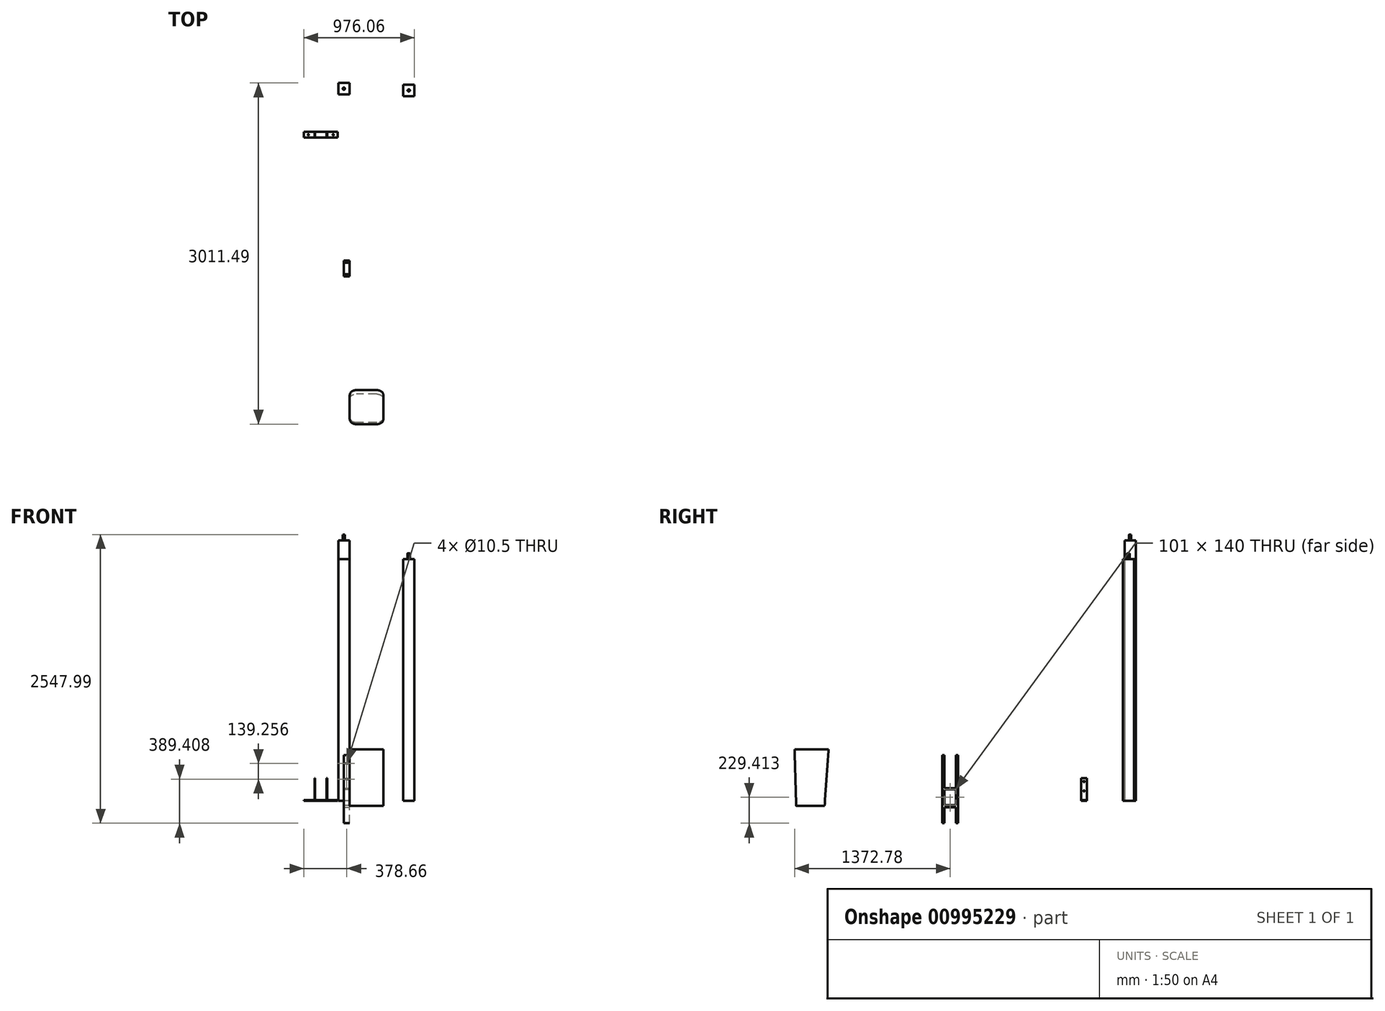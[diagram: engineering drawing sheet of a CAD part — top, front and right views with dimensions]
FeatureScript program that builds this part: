
annotation { "Feature Type Name" : "Feature", "Feature Type Description" : "" }
export const myFeature = defineFeature(function(context is Context, id is Id, definition is map)
    precondition{}
    {
        {
            var Q0;
            Q0=qCreatedBy(makeId("Top.planeOp"),FACE);
            var sketch = newSketch(context, id + "F0", { "sketchPlane" : qUnion([Q0])});
            skLineSegment(sketch, "E0.bottom", {"start": v(50, -50) * mm, "end": v(-50, -50) * mm});
            skLineSegment(sketch, "E0.top", {"start": v(50, 50) * mm, "end": v(-50, 50) * mm});
            skLineSegment(sketch, "E0.left", {"start": v(50, -50) * mm, "end": v(50, 50) * mm});
            skLineSegment(sketch, "E0.right", {"start": v(-50, -50) * mm, "end": v(-50, 50) * mm});
            skPoint(sketch, "E0.middle", {"position": v(0, 0) * mm});
            skLineSegment(sketch, "E1.bottom", {"start": v(522.4, 34.47) * mm, "end": v(622.4, 34.47) * mm});
            skLineSegment(sketch, "E1.top", {"start": v(522.4, -65.53) * mm, "end": v(622.4, -65.53) * mm});
            skLineSegment(sketch, "E1.left", {"start": v(522.4, 34.47) * mm, "end": v(522.4, -65.53) * mm});
            skLineSegment(sketch, "E1.right", {"start": v(622.4, 34.47) * mm, "end": v(622.4, -65.53) * mm});
            skSolve(sketch);
        }
        {
            var Q0;
            Q0=makeQuery(id+"F0.imprint","IMPRINT",FACE,{"disambiguationData":[TD([[makeQuery(id+"F0.imprint","IMPRINT",EDGE,{"derivedFrom":sQuery(id+"F0.wireOp",EDGE,"E0.bottom")}),-1.0]])]});
            extrude(context, id + "F1", {"entities" : qUnion([Q0]), "depth" : 2300 * mm, "offsetDistance" : 25 * mm});
        }
        {
            var Q0;
            Q0 = qSketchRegion(id + "F0", true);
            extrude(context, id + "F2", {"entities" : qUnion([Q0]), "depth" : 2135 * mm, "offsetDistance" : 25 * mm});
        }
        {
            var Q0;
            Q0=makeQuery(id+"F1.opExtrude","CAP_FACE",FACE,{"disambiguationData":[OSD([sQuery(id+"F0.wireOp",EDGE,"E0.bottom"),sQuery(id+"F0.wireOp",EDGE,"E0.top"),sQuery(id+"F0.wireOp",EDGE,"E0.left"),sQuery(id+"F0.wireOp",EDGE,"E0.right")])],"isStart":false});
            var sketch = newSketch(context, id + "F3", { "sketchPlane" : qUnion([Q0])});
            skCircle(sketch, "E2", {"center": v(0, 0) * mm, "radius": 10 * mm});
            skSolve(sketch);
        }
        {
            var Q0;
            Q0=makeQuery(id+"F3.imprint","IMPRINT",FACE,{"disambiguationData":[TD([[makeQuery(id+"F3.imprint","IMPRINT",EDGE,{"derivedFrom":sQuery(id+"F3.wireOp",EDGE,"E2")}),1.0]])]});
            extrude(context, id + "F4", {"entities" : qUnion([Q0]), "operationType" : NewBodyOperationType.ADD, "depth" : 50 * mm, "offsetDistance" : 25 * mm});
        }
        {
            var Q0;
            Q0=makeQuery(id+"F2.opExtrude","CAP_FACE",FACE,{"disambiguationData":[OSD([sQuery(id+"F0.wireOp",EDGE,"E1.bottom"),sQuery(id+"F0.wireOp",EDGE,"E1.top"),sQuery(id+"F0.wireOp",EDGE,"E1.left"),sQuery(id+"F0.wireOp",EDGE,"E1.right")])],"isStart":false});
            var sketch = newSketch(context, id + "F5", { "sketchPlane" : qUnion([Q0])});
            skCircle(sketch, "E3", {"center": v(572.4, -15.53) * mm, "radius": 10 * mm});
            skPoint(sketch, "E3.centerSnap0", {"position": v(522.4, -15.53) * mm});
            skPoint(sketch, "E3.centerSnap1", {"position": v(572.4, -65.53) * mm});
            skSolve(sketch);
        }
        {
            var Q0;
            Q0 = qSketchRegion(id + "F5", true);
            extrude(context, id + "F6", {"entities" : qUnion([Q0]), "operationType" : NewBodyOperationType.ADD, "depth" : 50 * mm, "offsetDistance" : 25 * mm});
        }
        {
            var Q0;
            Q0=qCreatedBy(makeId("Right.planeOp"),FACE);
            var sketch = newSketch(context, id + "F7", { "sketchPlane" : qUnion([Q0])});
            skLineSegment(sketch, "E4.bottom", {"start": v(-1658.7, 402.01) * mm, "end": v(-1518.7, 402.01) * mm});
            skLineSegment(sketch, "E4.top", {"start": v(-1658.7, -197.99) * mm, "end": v(-1518.7, -197.99) * mm});
            skLineSegment(sketch, "E4.left", {"start": v(-1658.7, 402.01) * mm, "end": v(-1658.7, -197.99) * mm});
            skLineSegment(sketch, "E4.right", {"start": v(-1518.7, 402.01) * mm, "end": v(-1518.7, -197.99) * mm});
            skSolve(sketch);
        }
        {
            var Q0;
            Q0=makeQuery(id+"F7.imprint","IMPRINT",FACE,{"disambiguationData":[TD([[makeQuery(id+"F7.imprint","IMPRINT",EDGE,{"derivedFrom":sQuery(id+"F7.wireOp",EDGE,"E4.bottom")}),-1.0]])]});
            extrude(context, id + "F8", {"entities" : qUnion([Q0]), "depth" : 50 * mm, "offsetDistance" : 25 * mm});
        }
        {
            var Q0;
            Q0=makeQuery(id+"F8.opExtrude","CAP_FACE",FACE,{"disambiguationData":[OSD([sQuery(id+"F7.wireOp",EDGE,"E4.bottom"),sQuery(id+"F7.wireOp",EDGE,"E4.top"),sQuery(id+"F7.wireOp",EDGE,"E4.left"),sQuery(id+"F7.wireOp",EDGE,"E4.right")])],"isStart":false});
            var sketch = newSketch(context, id + "F9", { "sketchPlane" : qUnion([Q0])});
            skLineSegment(sketch, "E5", {"start": v(-1588.7, 427.22) * mm, "end": v(-1588.7, -231.36) * mm, "construction": true});
            skPoint(sketch, "E5.startSnap0", {"position": v(-1588.7, 402.01) * mm});
            skLineSegment(sketch, "E6", {"start": v(-1690.33, 102.01) * mm, "end": v(-1494.55, 102.01) * mm, "construction": true});
            skPoint(sketch, "E6.startSnap0", {"position": v(-1658.7, 102.01) * mm});
            skPoint(sketch, "E7.middle", {"position": v(-1588.7, 284.64) * mm});
            skLineSegment(sketch, "E8", {"start": v(-1639.2, 402.01) * mm, "end": v(-1639.2, 111.41) * mm});
            skLineSegment(sketch, "E9", {"start": v(-1639.2, 111.41) * mm, "end": v(-1538.2, 111.41) * mm});
            skLineSegment(sketch, "E10", {"start": v(-1538.2, 111.41) * mm, "end": v(-1538.2, 402.01) * mm});
            skLineSegment(sketch, "E11", {"start": v(-1538.2, 402.01) * mm, "end": v(-1639.2, 402.01) * mm});
            skLineSegment(sketch, "E12", {"start": v(-1588.7, 418.52) * mm, "end": v(-1588.7, 132.47) * mm, "construction": true});
            skLineSegment(sketch, "E13", {"start": v(-1639.2, -197.99) * mm, "end": v(-1639.2, -57.99) * mm});
            skLineSegment(sketch, "E14", {"start": v(-1639.2, -57.99) * mm, "end": v(-1538.2, -57.99) * mm});
            skLineSegment(sketch, "E15", {"start": v(-1538.2, -57.99) * mm, "end": v(-1538.2, -197.99) * mm});
            skLineSegment(sketch, "E16", {"start": v(-1588.7, -57.99) * mm, "end": v(-1588.7, -234) * mm, "construction": true});
            skLineSegment(sketch, "E17.bottom", {"start": v(-1639.2, 101.42) * mm, "end": v(-1538.2, 101.42) * mm});
            skLineSegment(sketch, "E17.top", {"start": v(-1639.2, -38.58) * mm, "end": v(-1538.2, -38.58) * mm});
            skLineSegment(sketch, "E17.left", {"start": v(-1639.2, 101.42) * mm, "end": v(-1639.2, -38.58) * mm});
            skLineSegment(sketch, "E17.right", {"start": v(-1538.2, 101.42) * mm, "end": v(-1538.2, -38.58) * mm});
            skLineSegment(sketch, "E18", {"start": v(-1588.7, 101.42) * mm, "end": v(-1588.7, -38.58) * mm, "construction": true});
            skLineSegment(sketch, "E19", {"start": v(-2961.49, 454.13) * mm, "end": v(-2661.49, 454.13) * mm});
            skLineSegment(sketch, "E20", {"start": v(-2661.49, 454.13) * mm, "end": v(-2696.45, -45.87) * mm});
            skLineSegment(sketch, "E21", {"start": v(-2696.45, -45.87) * mm, "end": v(-2946.45, -45.87) * mm});
            skLineSegment(sketch, "E22", {"start": v(-2946.45, -45.87) * mm, "end": v(-2961.49, 454.13) * mm});
            skSolve(sketch);
        }
        {
            var Q0;
            Q0=makeQuery(id+"F9.imprint","IMPRINT",FACE,{"disambiguationData":[TD([[makeQuery(id+"F9.imprint","IMPRINT",EDGE,{"derivedFrom":sQuery(id+"F9.wireOp",EDGE,"E8")}),1.0]])]});
            var Q1;
            Q1=makeQuery(id+"F9.imprint","IMPRINT",FACE,{"disambiguationData":[TD([[makeQuery(id+"F9.imprint","IMPRINT",EDGE,{"derivedFrom":sQuery(id+"F9.wireOp",EDGE,"E17.bottom")}),-1.0]])]});
            var Q2;
            {var subQ0=sQuery(id+"F9.wireOp",EDGE,"E13");Q2=makeQuery(id+"F9.imprint","IMPRINT",FACE,{"disambiguationData":[TD([[makeQuery(id+"F9.imprint","IMPRINT",EDGE,{"derivedFrom":subQ0}),-1.0]])]});}
            extrude(context, id + "F10", {"entities" : qUnion([Q0, Q1, Q2]), "operationType" : NewBodyOperationType.REMOVE, "endBound" : BoundingType.THROUGH_ALL, "oppositeDirection" : true, "depth" : 25 * mm, "offsetDistance" : 25 * mm});
        }
        {
            var Q0;
            Q0=makeQuery(id+"F9.imprint","IMPRINT",FACE,{"disambiguationData":[TD([[makeQuery(id+"F9.imprint","IMPRINT",EDGE,{"derivedFrom":sQuery(id+"F9.wireOp",EDGE,"E19")}),-1.0]])]});
            extrude(context, id + "F11", {"entities" : qUnion([Q0]), "depth" : 300 * mm, "offsetDistance" : 25 * mm});
        }
        {
            var Q0;
            Q0=makeQuery(id+"F11.opExtrude","CAP_EDGE",EDGE,{"disambiguationData":[OSD([sQuery(id+"F9.wireOp",EDGE,"E22")])],"isStart":false});
            var Q1;
            Q1=makeQuery(id+"F11.opExtrude","CAP_EDGE",EDGE,{"disambiguationData":[OSD([sQuery(id+"F9.wireOp",EDGE,"E22")])],"isStart":true});
            var Q2;
            Q2=makeQuery(id+"F11.opExtrude","CAP_EDGE",EDGE,{"disambiguationData":[OSD([sQuery(id+"F9.wireOp",EDGE,"E20")])],"isStart":true});
            var Q3;
            Q3=makeQuery(id+"F11.opExtrude","CAP_EDGE",EDGE,{"disambiguationData":[OSD([sQuery(id+"F9.wireOp",EDGE,"E20")])],"isStart":false});
            fillet(context, id + "F12", {"entities" : qUnion([Q0, Q1, Q2, Q3]), "radius" : 60 * mm, "rho" : 0.5, "crossSection" : FilletCrossSection.CONIC, "allowEdgeOverflow" : false});
        }
        {
            var Q0;
            Q0=makeQuery(id+"F8.opExtrude","SWEPT_FACE",FACE,{"disambiguationData":[OSD([sQuery(id+"F7.wireOp",EDGE,"E4.left")])]});
            var sketch = newSketch(context, id + "F13", { "sketchPlane" : qUnion([Q0])});
            skPoint(sketch, "E23.centerSnap0", {"position": v(25, 402.01) * mm});
            skPoint(sketch, "E24", {"position": v(25, 330.67) * mm});
            skPoint(sketch, "E25", {"position": v(25, 191.42) * mm});
            skSolve(sketch);
        }
        {
            var Q0;
            Q0=qCreatedBy(makeId("Top.planeOp"),FACE);
            var sketch = newSketch(context, id + "F14", { "sketchPlane" : qUnion([Q0])});
            skLineSegment(sketch, "E26.bottom", {"start": v(-53.66, -432.35) * mm, "end": v(-353.66, -432.35) * mm});
            skLineSegment(sketch, "E26.top", {"start": v(-53.66, -382.35) * mm, "end": v(-353.66, -382.35) * mm});
            skLineSegment(sketch, "E26.left", {"start": v(-53.66, -432.35) * mm, "end": v(-53.66, -382.35) * mm});
            skLineSegment(sketch, "E26.right", {"start": v(-353.66, -432.35) * mm, "end": v(-353.66, -382.35) * mm});
            skPoint(sketch, "E26.middle", {"position": v(-203.66, -407.35) * mm});
            skPoint(sketch, "E27", {"position": v(-313.66, -407.35) * mm});
            skPoint(sketch, "E27.positionSnap0", {"position": v(-353.66, -407.35) * mm});
            skPoint(sketch, "E28", {"position": v(-93.66, -407.35) * mm});
            skSolve(sketch);
        }
        {
            var Q0;
            Q0=makeQuery(id+"F14.imprint","IMPRINT",FACE,{"disambiguationData":[TD([[makeQuery(id+"F14.imprint","IMPRINT",EDGE,{"derivedFrom":sQuery(id+"F14.wireOp",EDGE,"E26.bottom")}),-1.0]])]});
            extrude(context, id + "F15", {"entities" : qUnion([Q0]), "depth" : 200 * mm, "offsetDistance" : 25 * mm});
        }
        {
            var Q0;
            Q0=makeQuery(id+"F15.opExtrude","SWEPT_FACE",FACE,{"disambiguationData":[OSD([sQuery(id+"F14.wireOp",EDGE,"E26.bottom")])]});
            var sketch = newSketch(context, id + "F16", { "sketchPlane" : qUnion([Q0])});
            skLineSegment(sketch, "E29.bottom", {"start": v(-353.66, 200) * mm, "end": v(-259.16, 200) * mm});
            skLineSegment(sketch, "E29.top", {"start": v(-353.66, 5) * mm, "end": v(-259.16, 5) * mm});
            skLineSegment(sketch, "E29.left", {"start": v(-353.66, 200) * mm, "end": v(-353.66, 5) * mm});
            skLineSegment(sketch, "E29.right", {"start": v(-259.16, 200) * mm, "end": v(-259.16, 5) * mm});
            skLineSegment(sketch, "E30.bottom", {"start": v(-53.66, 200) * mm, "end": v(-148.16, 200) * mm});
            skLineSegment(sketch, "E30.top", {"start": v(-53.66, 5) * mm, "end": v(-148.16, 5) * mm});
            skLineSegment(sketch, "E30.left", {"start": v(-53.66, 200) * mm, "end": v(-53.66, 5) * mm});
            skLineSegment(sketch, "E30.right", {"start": v(-148.16, 200) * mm, "end": v(-148.16, 5) * mm});
            skLineSegment(sketch, "E31.bottom", {"start": v(-254.16, 200) * mm, "end": v(-153.16, 200) * mm});
            skLineSegment(sketch, "E31.top", {"start": v(-254.16, 5) * mm, "end": v(-153.16, 5) * mm});
            skLineSegment(sketch, "E31.left", {"start": v(-153.16, 200) * mm, "end": v(-153.16, 5) * mm});
            skLineSegment(sketch, "E31.right", {"start": v(-254.16, 200) * mm, "end": v(-254.16, 5) * mm});
            skLineSegment(sketch, "E32", {"start": v(-203.66, 200) * mm, "end": v(-203.66, 0) * mm, "construction": true});
            skLineSegment(sketch, "E33", {"start": v(-203.66, 200) * mm, "end": v(-203.66, 5) * mm, "construction": true});
            skSolve(sketch);
        }
        {
            var Q0;
            Q0=makeQuery(id+"F16.imprint","IMPRINT",FACE,{"disambiguationData":[TD([[makeQuery(id+"F16.imprint","IMPRINT",EDGE,{"derivedFrom":sQuery(id+"F16.wireOp",EDGE,"E29.bottom")}),1.0]])]});
            var Q1;
            Q1=makeQuery(id+"F16.imprint","IMPRINT",FACE,{"disambiguationData":[TD([[makeQuery(id+"F16.imprint","IMPRINT",EDGE,{"derivedFrom":sQuery(id+"F16.wireOp",EDGE,"E31.bottom")}),1.0]])]});
            var Q2;
            Q2=makeQuery(id+"F16.imprint","IMPRINT",FACE,{"disambiguationData":[TD([[makeQuery(id+"F16.imprint","IMPRINT",EDGE,{"derivedFrom":sQuery(id+"F16.wireOp",EDGE,"E30.bottom")}),1.0]])]});
            extrude(context, id + "F17", {"entities" : qUnion([Q0, Q1, Q2]), "operationType" : NewBodyOperationType.REMOVE, "endBound" : BoundingType.THROUGH_ALL, "oppositeDirection" : true, "depth" : 25 * mm, "offsetDistance" : 25 * mm});
        }
        {
            var Q0;
            Q0=makeQuery(id+"F17.boolean.opBoolean","COPY",FACE,{"derivedFrom":makeQuery(id+"F17.opExtrude","SWEPT_FACE",FACE,{"disambiguationData":[OSD([sQuery(id+"F16.wireOp",EDGE,"E29.right")])]})});
            var sketch = newSketch(context, id + "F18", { "sketchPlane" : qUnion([Q0])});
            skPoint(sketch, "E34.centerSnap0", {"position": v(407.35, 200) * mm});
            skPoint(sketch, "E35", {"position": v(407.35, 170.62) * mm});
            skPoint(sketch, "E36", {"position": v(407.35, 87.65) * mm});
            skSolve(sketch);
        }
        {
            var Q0;
            Q0=sQuery(id+"F13.wireOp",VERTEX,"E24");
            var Q1;
            Q1=sQuery(id+"F13.wireOp",VERTEX,"E25");
            var Q2;
            Q2=makeQuery(id+"F8.opExtrude","SWEPT_BODY",BODY,{"disambiguationData":[OSD([sQuery(id+"F7.wireOp",EDGE,"E4.bottom"),sQuery(id+"F7.wireOp",EDGE,"E4.top"),sQuery(id+"F7.wireOp",EDGE,"E4.left"),sQuery(id+"F7.wireOp",EDGE,"E4.right")])]});
            hole(context, id + "F19", {"style" : HoleStyle.SIMPLE, "endStyle" : HoleEndStyle.THROUGH, "standardTappedOrClearance" : lookupTablePath({ "standard" : "ISO", "size" : "10.5", "type" : "Drilled" }), "standardBlindInLast" : lookupTablePath({ "standard" : "ISO", "size" : "10.5", "type" : "Drilled" }), "holeDiameter" : 10.5 * mm, "majorDiameter" : 5 * mm, "isTappedThrough" : true, "tappedDepth" : 12 * mm, "tapClearance" : 3, "locations" : qUnion([Q0, Q1]), "scope" : qUnion([Q2])});
        }
        {
            var Q0;
            Q0=sQuery(id+"F14.wireOp",VERTEX,"E27");
            var Q1;
            Q1=sQuery(id+"F14.wireOp",VERTEX,"E28");
            var Q2;
            Q2=makeQuery(id+"F15.opExtrude","SWEPT_BODY",BODY,{"disambiguationData":[OSD([sQuery(id+"F14.wireOp",EDGE,"E26.bottom"),sQuery(id+"F14.wireOp",EDGE,"E26.top"),sQuery(id+"F14.wireOp",EDGE,"E26.left"),sQuery(id+"F14.wireOp",EDGE,"E26.right")])]});
            hole(context, id + "F20", {"style" : HoleStyle.SIMPLE, "endStyle" : HoleEndStyle.THROUGH, "oppositeDirection" : true, "standardTappedOrClearance" : lookupTablePath({ "standard" : "ISO", "size" : "10.5", "type" : "Drilled" }), "standardBlindInLast" : lookupTablePath({ "standard" : "ISO", "size" : "10.5", "type" : "Drilled" }), "holeDiameter" : 10.5 * mm, "majorDiameter" : 5 * mm, "isTappedThrough" : true, "tappedDepth" : 12 * mm, "tapClearance" : 3, "locations" : qUnion([Q0, Q1]), "scope" : qUnion([Q2])});
        }
        {
            var Q0;
            Q0=sQuery(id+"F18.wireOp",VERTEX,"E35");
            var Q1;
            Q1=sQuery(id+"F18.wireOp",VERTEX,"E36");
            var Q2;
            Q2=makeQuery(id+"F15.opExtrude","SWEPT_BODY",BODY,{"disambiguationData":[OSD([sQuery(id+"F14.wireOp",EDGE,"E26.bottom"),sQuery(id+"F14.wireOp",EDGE,"E26.top"),sQuery(id+"F14.wireOp",EDGE,"E26.left"),sQuery(id+"F14.wireOp",EDGE,"E26.right")])]});
            hole(context, id + "F21", {"style" : HoleStyle.SIMPLE, "endStyle" : HoleEndStyle.THROUGH, "standardTappedOrClearance" : lookupTablePath({ "standard" : "ISO", "size" : "10.5", "type" : "Drilled" }), "standardBlindInLast" : lookupTablePath({ "standard" : "ISO", "size" : "10.5", "type" : "Drilled" }), "holeDiameter" : 10.5 * mm, "majorDiameter" : 5 * mm, "isTappedThrough" : true, "tappedDepth" : 12 * mm, "tapClearance" : 3, "locations" : qUnion([Q0, Q1]), "scope" : qUnion([Q2])});
        }
    });
